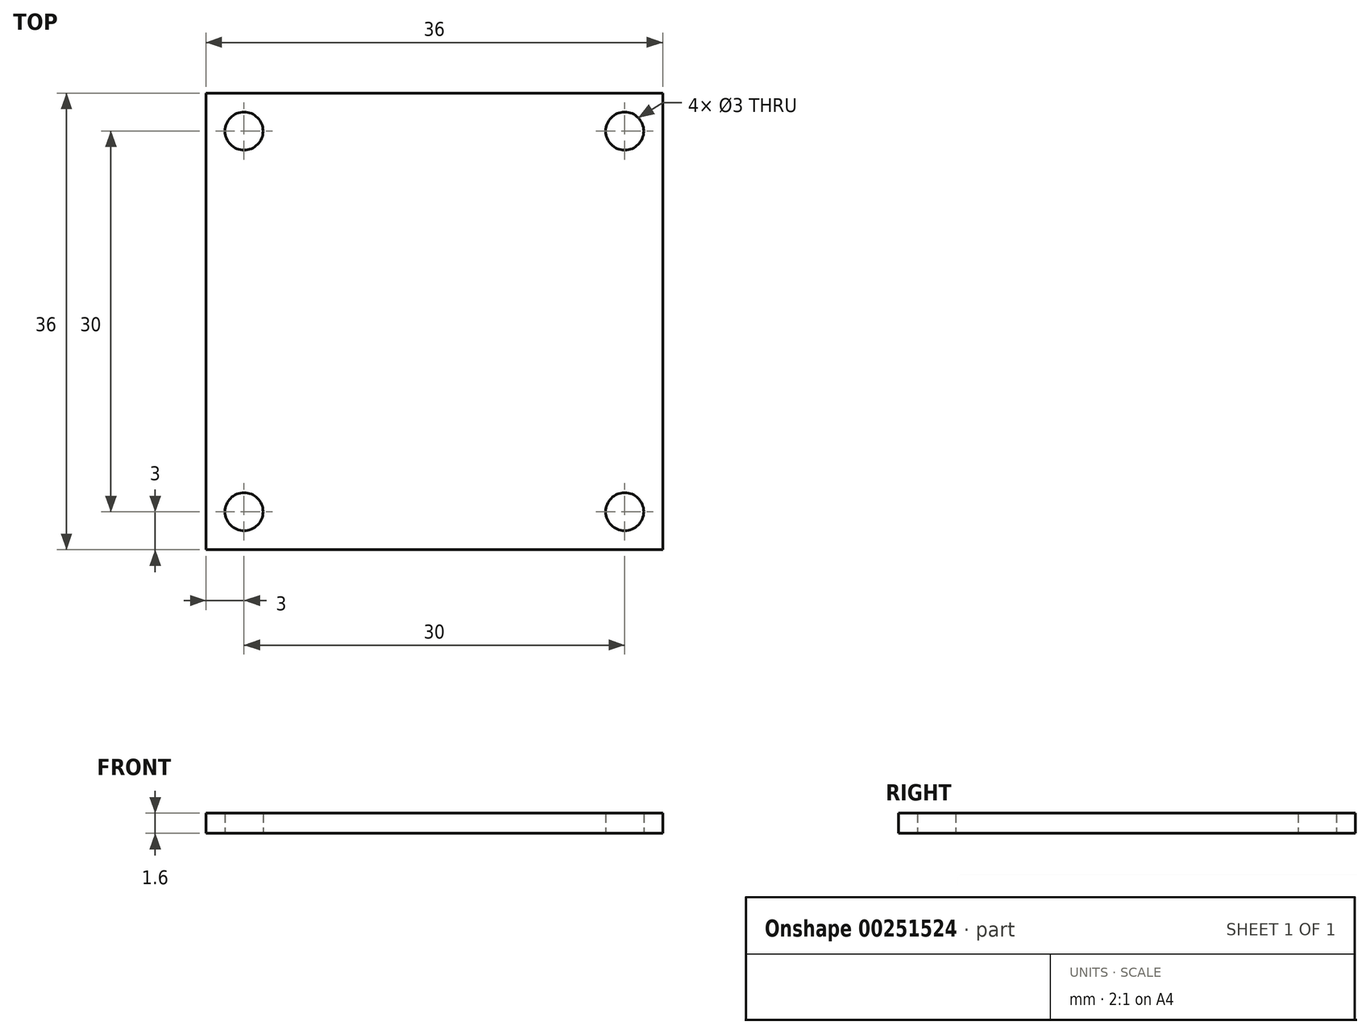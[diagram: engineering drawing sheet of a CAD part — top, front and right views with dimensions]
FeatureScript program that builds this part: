
annotation { "Feature Type Name" : "Feature", "Feature Type Description" : "" }
export const myFeature = defineFeature(function(context is Context, id is Id, definition is map)
    precondition{}
    {
        {
            var Q0;
            Q0=qCreatedBy(makeId("Top.planeOp"),FACE);
            var sketch = newSketch(context, id + "F0", { "sketchPlane" : qUnion([Q0])});
            skLineSegment(sketch, "E0.bottom", {"start": v(18, 18) * mm, "end": v(-18, 18) * mm});
            skLineSegment(sketch, "E0.top", {"start": v(18, -18) * mm, "end": v(-18, -18) * mm});
            skLineSegment(sketch, "E0.left", {"start": v(18, 18) * mm, "end": v(18, -18) * mm});
            skLineSegment(sketch, "E0.right", {"start": v(-18, 18) * mm, "end": v(-18, -18) * mm});
            skPoint(sketch, "E0.middle", {"position": v(0, 0) * mm});
            skCircle(sketch, "E1", {"center": v(-15, 15) * mm, "radius": 1.5 * mm});
            skCircle(sketch, "E2", {"center": v(15, 15) * mm, "radius": 1.5 * mm});
            skCircle(sketch, "E3", {"center": v(15, -15) * mm, "radius": 1.5 * mm});
            skCircle(sketch, "E4", {"center": v(-15, -15) * mm, "radius": 1.5 * mm});
            skSolve(sketch);
        }
        {
            var Q0;
            Q0=makeQuery(id+"F0.imprint","IMPRINT",FACE,{"disambiguationData":[TD([[makeQuery(id+"F0.imprint","IMPRINT",EDGE,{"derivedFrom":sQuery(id+"F0.wireOp",EDGE,"E0.bottom")}),1.0]])]});
            extrude(context, id + "F1", {"entities" : qUnion([Q0]), "depth" : 1.6 * mm});
        }
    });
